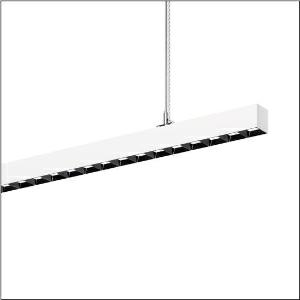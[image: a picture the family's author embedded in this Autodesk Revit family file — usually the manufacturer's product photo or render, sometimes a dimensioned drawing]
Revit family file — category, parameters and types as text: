
# Revit family: silica_r__21_51mx34dc4dwb_1888
name_source: partatom
category: Lighting Fixtures
units: mm (PartAtom-declared; Revit-internal decimal feet)

## family parameters
Cut with Voids When Loaded = No
Host = Face
Light Source = No
Part Type = Normal
Room Calculation Point = No
Round Connector Dimension = Use Diameter
Shared = No

## types (1)
- --- (1 x LED, 19200 lm, 120.3 W, 4000K)
    Apparent Load = 120 VA
    CIE Flux Codes = 74 94 99 56 100
    Color Rendering = 80
    Color Temperature = 4000K
    Default Elevation = 1800 mm
    Description = Silica® 21, office luminaire, primary light control with darklight reflector, of PMMA, black, light emission: direct/indirect distribution, primary light characteristic: asymmetric, installation type: suspended mounting, LED, rated luminous flux: 19.200lm, luminous efficacy: 160lm/W, light colour: 840, colour temperature: 4000K, with terminal, 3+2-pole, max. 2.5mm², mains connection: 220..240V, AC, 50/60Hz, rated input power: 120.3W, luminaire housing, of aluminium, traffic white (RAL 9016), length: 3.004mm, width: 53mm, height: 53mm, protection rating (complete): IP20, insulation class (complete): insulation class I (protective earthing), certification: CE, permissible operating ambient temperature: 0..+35°C, standard: EN 50419, packaging unit: 1 piece
    Height = 53 mm
    Lamp = 1 x LED
    Lamp Light Flux = 19200 lm
    Lamp Power = 120.3 W
    Lamp count = 1
    Length = 3004 mm
    Luminous efficacy = 160 lm/W
    Manufacturer = Siteco
    ModVariant = No
    Model = 51MX34DC4DWB
    Mounting Place = Ceiling
    Mounting Type = Pendant
    Number of Poles = 1
    OnlyDefault = Yes
    Power Factor = 1
    Product Name = Silica® 21
    Product group = office luminaire | ceiling pendant
    ProductGroupID = 902
    Protection Class = Protection class I
    Protection Degree = IP 20
    RLX_Detail_Level = 1
    RLX_Emergency_Light_Flux = 0 lm
    RLX_Emergency_Type = 0
    RLX_Emergency_Type_DB = No
    RlxData = <blob elided: 64881 chars, md5=82b62aaa>
    Socket = socket
    Standby Power = 0 W
    System Light Flux = 19200 lm
    System Power = 120 W
    Type Comments = factory setting: luminous flux: 100 % | dim-lin: 254 | 418 mA
    Type Image = l_1297801.jpg
    URL = http://relux.com
    VarID = @adj_050999
    Voltage = 0 V
    Weight = 0.00 kg
    Width = 53 mm

## geometry (parser evidence)
native form markers: Blend x4, Sweep x11
no freeform markers — native parametric forms only
